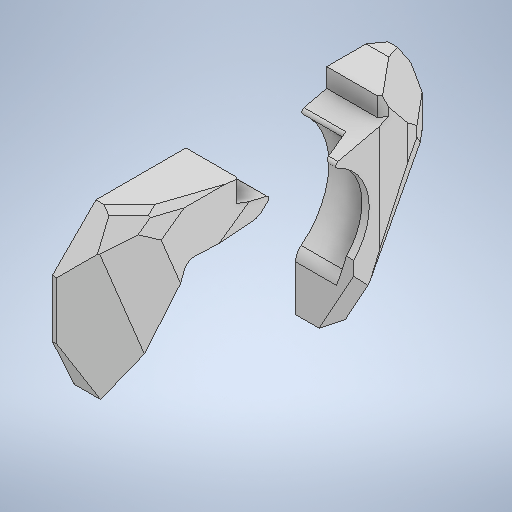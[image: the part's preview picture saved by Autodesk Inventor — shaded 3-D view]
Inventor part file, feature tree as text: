
AUTODESK INVENTOR PART (.ipt)
format: ipt  version: 2025.2 (Build 292293000, 293)  size: 781,312 bytes
history: native  units: in
note: dims shown in document units (in); Inventor stores cm internally (conversion verified against a paired STEP export)
features: other x2, extrude x1, mirror x1, sketch x1
ambient origin geometry x8: Origin, YZ Plane, XZ Plane, XY Plane, X Axis, Y Axis, Z Axis, Center Point
bodies: body_side (feature_tree), Solid2 (feature_tree)
feature tree (5):
  extrude  "Extrusion1"  Depth=0.2362in
  mirror  "Mirror1"
  other  "Solid2::body_side"
  other  "TaggingFeature1"
  sketch  "Sketch1"  dims[d0=0.3937in d1=0.1752in d2=0.1752in d3=0.1752in d6=0.1752in d7=0.1752in d8=0.1752in d9=0.2362in d10=0.0in]
